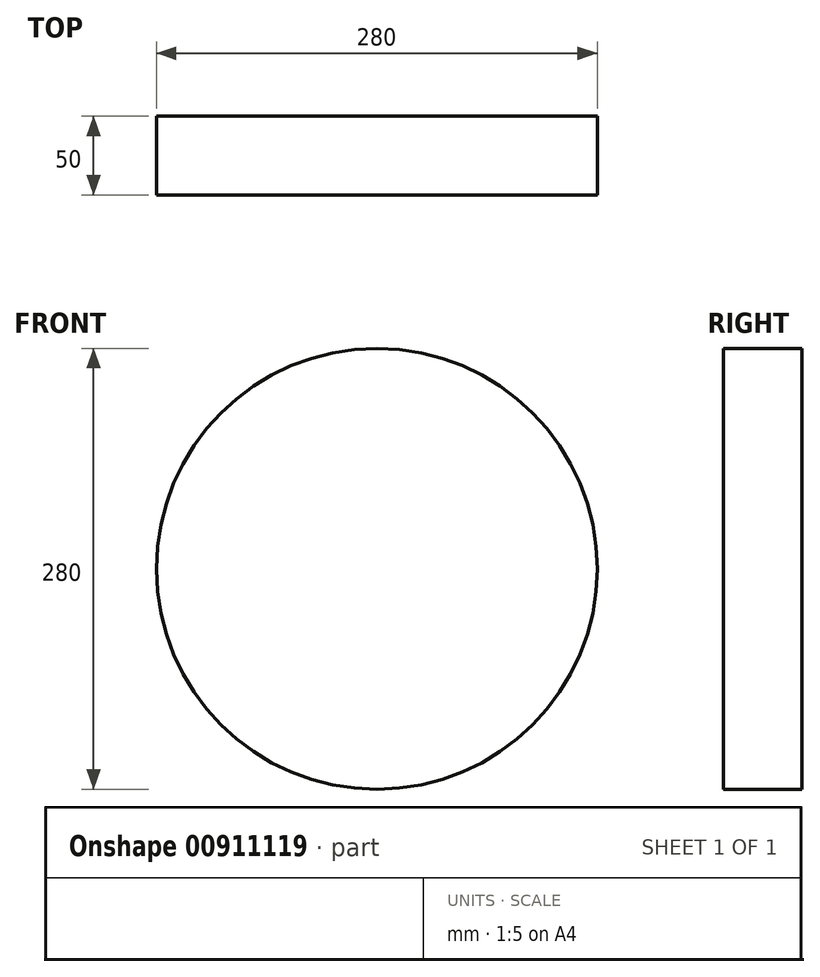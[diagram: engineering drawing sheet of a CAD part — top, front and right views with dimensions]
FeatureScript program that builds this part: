
annotation { "Feature Type Name" : "Feature", "Feature Type Description" : "" }
export const myFeature = defineFeature(function(context is Context, id is Id, definition is map)
    precondition{}
    {
        {
            var Q0;
            Q0=qCreatedBy(makeId("Front.planeOp"),FACE);
            var sketch = newSketch(context, id + "F0", { "sketchPlane" : qUnion([Q0])});
            skCircle(sketch, "E0", {"center": v(0, 0) * mm, "radius": 140 * mm});
            skSolve(sketch);
        }
        {
            var Q0;
            Q0=makeQuery(id+"F0.imprint","IMPRINT",FACE,{"disambiguationData":[TD([[makeQuery(id+"F0.imprint","IMPRINT",EDGE,{"derivedFrom":sQuery(id+"F0.wireOp",EDGE,"E0")}),1.0]])]});
            extrude(context, id + "F1", {"entities" : qUnion([Q0]), "depth" : 50 * mm, "offsetDistance" : 25 * mm});
        }
    });
